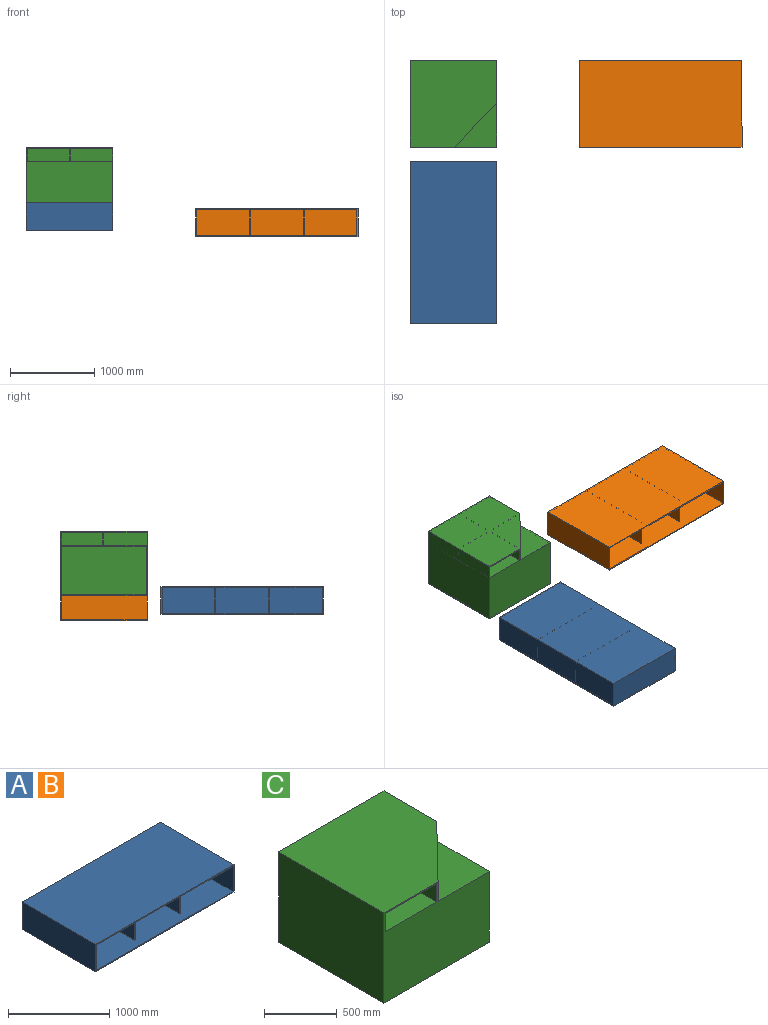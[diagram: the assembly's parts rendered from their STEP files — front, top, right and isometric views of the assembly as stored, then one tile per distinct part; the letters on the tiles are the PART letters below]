
ASSEMBLY  parts=3 mates=2
PART A: 19 faces, bbox 1930.4x1028.7x330.2 mm
  f0: plane 1905x1016mm, normal (0,0,1), area 1912254.2mm2, adj f1,f2,f3,f4,f5,f6,f10,f13
  f1: plane 1016x304.8mm, normal (1,0,0), area 309676.8mm2, adj f0,f7,f10,f16
  f2: plane 1016x304.8mm, normal (-1,0,0), area 309676.8mm2, adj f0,f7,f10,f18
  f3: plane 914.4x304.8mm, normal (1,0,0), area 278709.1mm2, adj f0,f7,f13,f17
  f4: plane 914.4x304.8mm, normal (-1,0,0), area 278709.1mm2, adj f0,f7,f13,f16
  f5: plane 914.4x304.8mm, normal (1,0,0), area 278709.1mm2, adj f0,f7,f14,f18
  f6: plane 914.4x304.8mm, normal (-1,0,0), area 278709.1mm2, adj f0,f7,f14,f17
  f7: plane 1905x1016mm, normal (0,0,-1), area 1912254.2mm2, adj f1,f2,f3,f4,f5,f6,f10,f13
  f8: plane 1930.4x330.2mm, normal (0,1,0), area 637418.1mm2, adj f9,f11,f12,f15
  f9: plane 1028.7x330.2mm, normal (-1,0,0), area 339676.7mm2, adj f8,f10,f12,f15
  f10: plane 1930.4x330.2mm, normal (0,-1,0), area 56774.1mm2, adj f0,f1,f2,f7,f9,f11,f12,f15
  f11: plane 1028.7x330.2mm, normal (1,0,0), area 339676.7mm2, adj f8,f10,f12,f15
  f12: plane 1930.4x1028.7mm, normal (0,0,-1), area 1985802.5mm2, adj f8,f9,f10,f11
  f13: plane 304.8x12.7mm, normal (0,-1,0), area 3871mm2, adj f0,f3,f4,f7
  f14: plane 304.8x12.7mm, normal (0,-1,0), area 3871mm2, adj f0,f5,f6,f7
  f15: plane 1930.4x1028.7mm, normal (0,0,1), area 1985802.5mm2, adj f8,f9,f10,f11
  f16: plane 626.36x304.8mm, normal (0,-1,0), area 190915.7mm2, adj f0,f1,f4,f7
  f17: plane 626.36x304.8mm, normal (0,-1,0), area 190915.7mm2, adj f0,f3,f6,f7
  f18: plane 626.87x304.8mm, normal (0,-1,0), area 191070.6mm2, adj f0,f2,f5,f7
PART B: same geometry as A
PART C: 33 faces, bbox 1028.7x1028.7x762 mm
  f0: plane 514.35x501.65mm, normal (0,0,1), area 258023.7mm2, adj f4,f5,f8,f15
  f1: plane 514.35x501.65mm, normal (0,0,1), area 258023.7mm2, adj f4,f12,f13,f14
  f2: plane 1028.7x762mm, normal (0,1,0), area 783869.4mm2, adj f3,f5,f6,f17
  f3: plane 1028.7x762mm, normal (-1,0,0), area 783869.4mm2, adj f2,f4,f6,f17
  f4: plane 1028.7x762mm, normal (0,-1,0), area 624595.5mm2, adj f0,f1,f3,f5,f6,f12,f14,f15
  f5: plane 1028.7x762mm, normal (1,0,0), area 624434.2mm2, adj f0,f2,f4,f6,f7,f8,f9,f11
  f6: plane 1028.7x1028.7mm, normal (0,0,-1), area 1058223.7mm2, adj f2,f3,f4,f5
  f7: plane 501.65x488.95mm, normal (0,0,1), area 245281.8mm2, adj f5,f9,f10,f11
  f8: plane 501.65x152.4mm, normal (0,-1,0), area 76451.5mm2, adj f0,f5,f15,f19
  f9: plane 501.65x152.4mm, normal (0,1,0), area 76451.5mm2, adj f5,f7,f10,f20
  f10: plane 488.95x152.4mm, normal (1,0,0), area 74516mm2, adj f7,f9,f11,f20
  f11: plane 501.65x152.4mm, normal (0,-1,0), area 76451.5mm2, adj f5,f7,f10,f20
  f12: plane 514.35x152.4mm, normal (1,0,0), area 78386.9mm2, adj f1,f4,f13,f16
  f13: plane 501.65x152.4mm, normal (0,-1,0), area 76451.5mm2, adj f1,f12,f14,f16
  f14: plane 514.35x152.4mm, normal (-1,0,0), area 78386.9mm2, adj f1,f4,f13,f16
  f15: plane 514.35x152.4mm, normal (1,0,0), area 78386.9mm2, adj f0,f4,f8,f19
  f16: plane 514.35x501.65mm, normal (0,0,-1), area 258023.7mm2, adj f4,f12,f13,f14
  f17: plane 1028.7x1028.7mm, normal (0,0,1), area 929211.9mm2, adj f2,f3,f4,f5,f18
  f18: plane 514.35x501.65mm, normal (0.72,-0.7,0), area 9124.7mm2, adj f4,f5,f17,f19
  f19: plane 514.35x501.65mm, normal (0,0,-1), area 129011.8mm2, adj f8,f15,f18
  f20: plane 501.65x488.95mm, normal (0,0,-1), area 245281.8mm2, adj f5,f9,f10,f11
  f21: plane 1003.3x1003.3mm, normal (0,0,1), area 1006610.9mm2, adj f22,f23,f24,f25
  f22: plane 1003.3x571.5mm, normal (0,1,0), area 573385.9mm2, adj f21,f23,f25,f26
  f23: plane 1003.3x571.5mm, normal (-1,0,0), area 573385.9mm2, adj f21,f22,f24,f26
  f24: plane 1003.3x571.5mm, normal (0,-1,0), area 573385.9mm2, adj f21,f23,f25,f26
  f25: plane 1003.3x571.5mm, normal (1,0,0), area 573385.9mm2, adj f21,f22,f24,f26
  f26: plane 1003.3x1003.3mm, normal (0,0,-1), area 1006610.9mm2, adj f22,f23,f24,f25
  f27: plane 501.65x488.95mm, normal (0,0,-1), area 245281.8mm2, adj f29,f30,f31,f32
  f28: plane 501.65x488.95mm, normal (0,0,1), area 245281.8mm2, adj f29,f30,f31,f32
  f29: plane 488.95x152.4mm, normal (-1,0,0), area 74516mm2, adj f27,f28,f30,f32
  f30: plane 501.65x152.4mm, normal (0,-1,0), area 76451.5mm2, adj f27,f28,f29,f31
  f31: plane 488.95x152.4mm, normal (1,0,0), area 74516mm2, adj f27,f28,f30,f32
  f32: plane 501.65x152.4mm, normal (0,1,0), area 76451.5mm2, adj f27,f28,f29,f31
PLACE A rot(axis=(0,0,1),90deg) t=(2275.55,-4340.16,-808.3)mm
PLACE B t=(3262.16,-2244.95,-880.68)mm
PLACE C t=(1246.85,-2244.95,-584.32)mm
MATE planar C.f5 <-> A.f10  axis (1,0,0) through (2275.55,-1726.31,-278.77)mm
MATE planar C.f4 <-> B.f10  axis (0,-1,0) through (1756.96,-2244.95,-278.65)mm
